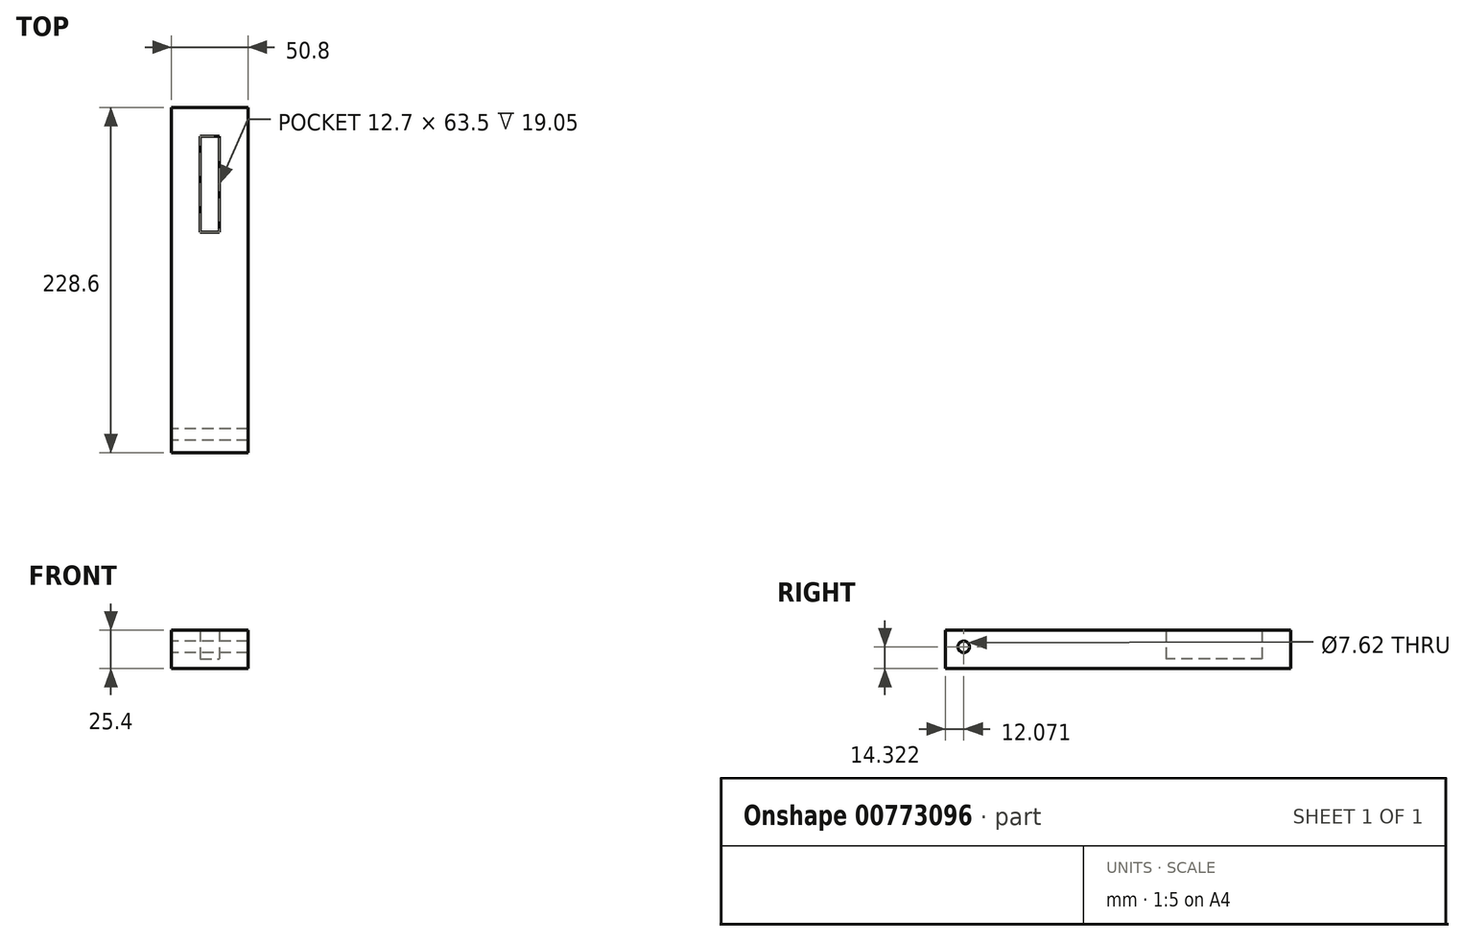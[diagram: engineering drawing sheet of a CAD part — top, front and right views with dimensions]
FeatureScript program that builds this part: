
annotation { "Feature Type Name" : "Feature", "Feature Type Description" : "" }
export const myFeature = defineFeature(function(context is Context, id is Id, definition is map)
    precondition{}
    {
        {
            var Q0;
            Q0=qCreatedBy(makeId("Top.planeOp"),FACE);
            var sketch = newSketch(context, id + "F0", { "sketchPlane" : qUnion([Q0])});
            skLineSegment(sketch, "E0.bottom", {"start": v(-64.12, 123.95) * mm, "end": v(-13.32, 123.95) * mm});
            skLineSegment(sketch, "E0.top", {"start": v(-64.12, -104.65) * mm, "end": v(-13.32, -104.65) * mm});
            skLineSegment(sketch, "E0.left", {"start": v(-64.12, 123.95) * mm, "end": v(-64.12, -104.65) * mm});
            skLineSegment(sketch, "E0.right", {"start": v(-13.32, 123.95) * mm, "end": v(-13.32, -104.65) * mm});
            skLineSegment(sketch, "E1.bottom", {"start": v(-45.07, 104.9) * mm, "end": v(-32.37, 104.9) * mm});
            skLineSegment(sketch, "E1.top", {"start": v(-45.07, 41.4) * mm, "end": v(-32.37, 41.4) * mm});
            skLineSegment(sketch, "E1.left", {"start": v(-45.07, 104.9) * mm, "end": v(-45.07, 41.4) * mm});
            skLineSegment(sketch, "E1.right", {"start": v(-32.37, 104.9) * mm, "end": v(-32.37, 41.4) * mm});
            skSolve(sketch);
        }
        {
            var Q0;
            Q0=makeQuery(id+"F0.imprint","IMPRINT",FACE,{"disambiguationData":[TD([[makeQuery(id+"F0.imprint","IMPRINT",EDGE,{"derivedFrom":sQuery(id+"F0.wireOp",EDGE,"E1.bottom")}),-1.0]])]});
            extrude(context, id + "F1", {"entities" : qUnion([Q0]), "depth" : 6.35 * mm, "offsetDistance" : 25.4 * mm});
        }
        {
            var Q0;
            Q0=makeQuery(id+"F0.imprint","IMPRINT",FACE,{"disambiguationData":[TD([[makeQuery(id+"F0.imprint","IMPRINT",EDGE,{"derivedFrom":sQuery(id+"F0.wireOp",EDGE,"E0.bottom")}),-1.0]])]});
            extrude(context, id + "F2", {"entities" : qUnion([Q0]), "operationType" : NewBodyOperationType.ADD, "depth" : 25.4 * mm, "offsetDistance" : 25.4 * mm});
        }
        {
            var Q0;
            Q0=makeQuery(id+"F2.opExtrude","SWEPT_FACE",FACE,{"disambiguationData":[OSD([sQuery(id+"F0.wireOp",EDGE,"E0.left")])]});
            var sketch = newSketch(context, id + "F3", { "sketchPlane" : qUnion([Q0])});
            skPoint(sketch, "E2", {"position": v(92.58, 14.32) * mm});
            skSolve(sketch);
        }
        {
            var Q0;
            Q0=sQuery(id+"F3.wireOp",VERTEX,"E2");
            var Q1;
            Q1=makeQuery(id+"F1.opExtrude","SWEPT_BODY",BODY,{"disambiguationData":[OSD([sQuery(id+"F0.wireOp",EDGE,"E1.bottom"),sQuery(id+"F0.wireOp",EDGE,"E1.top"),sQuery(id+"F0.wireOp",EDGE,"E1.left"),sQuery(id+"F0.wireOp",EDGE,"E1.right")])]});
            hole(context, id + "F4", {"style" : HoleStyle.SIMPLE, "endStyle" : HoleEndStyle.THROUGH, "holeDiameter" : 7.62 * mm, "majorDiameter" : 6.35 * mm, "isTappedThrough" : true, "tappedDepth" : 12.7 * mm, "tapClearance" : 3, "locations" : qUnion([Q0]), "scope" : qUnion([Q1])});
        }
    });
